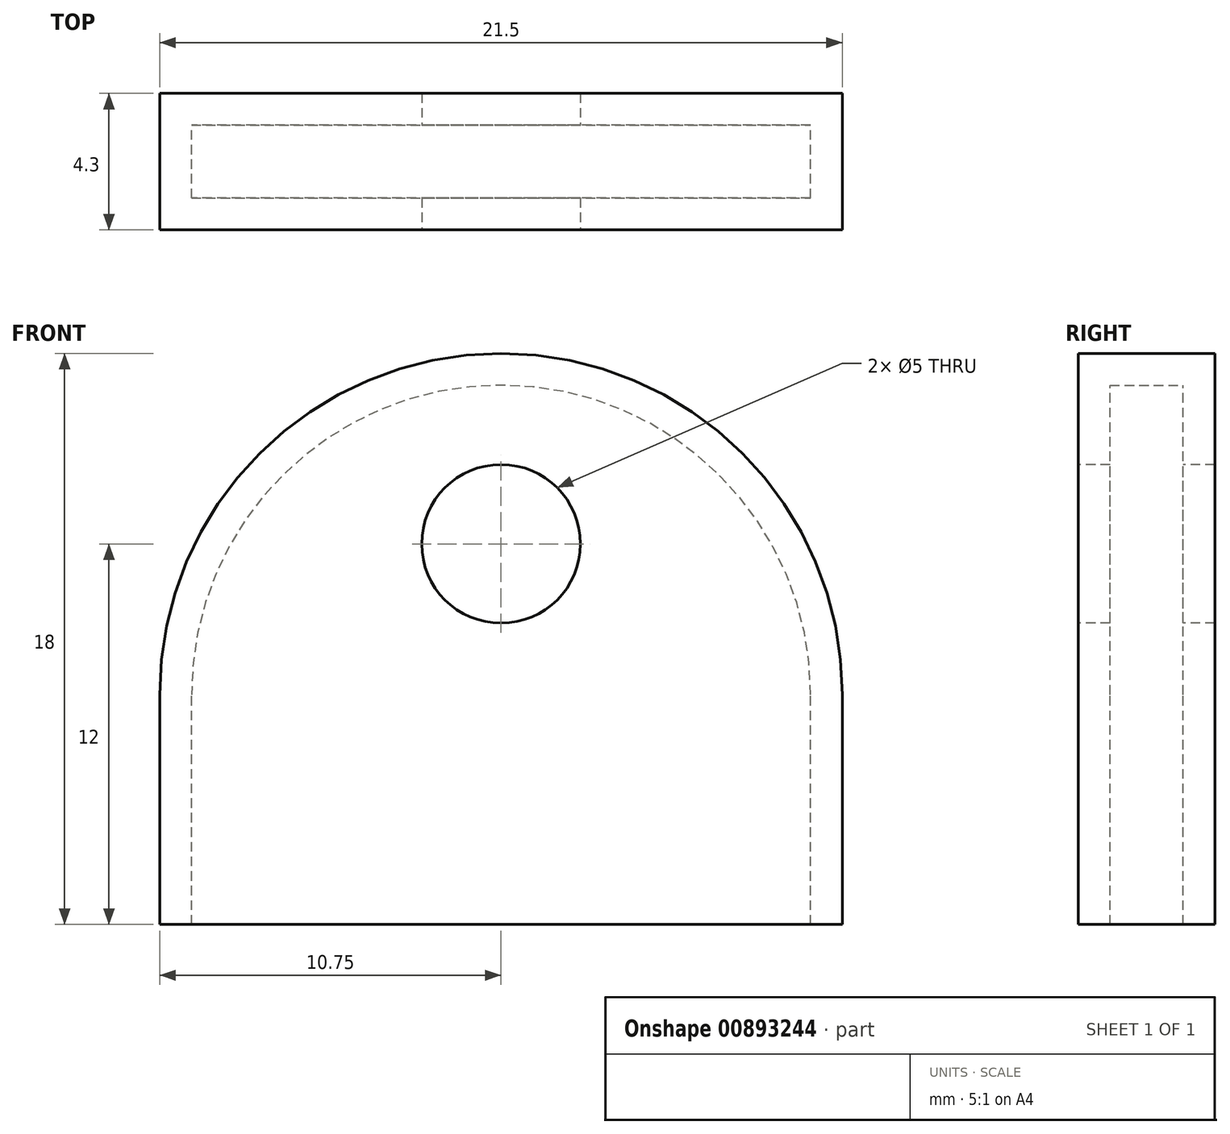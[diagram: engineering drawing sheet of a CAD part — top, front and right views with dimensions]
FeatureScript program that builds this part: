
annotation { "Feature Type Name" : "Feature", "Feature Type Description" : "" }
export const myFeature = defineFeature(function(context is Context, id is Id, definition is map)
    precondition{}
    {
        {
            var Q0;
            Q0=qCreatedBy(makeId("Front.planeOp"),FACE);
            var sketch = newSketch(context, id + "F0", { "sketchPlane" : qUnion([Q0])});
            skLineSegment(sketch, "E0.bottom", {"start": v(0, 0) * mm, "end": v(21.5, 0) * mm});
            skLineSegment(sketch, "E0.top", {"start": v(0, 7.25) * mm, "end": v(21.5, 7.25) * mm});
            skLineSegment(sketch, "E0.left", {"start": v(0, 0) * mm, "end": v(0, 7.25) * mm});
            skLineSegment(sketch, "E0.right", {"start": v(21.5, 0) * mm, "end": v(21.5, 7.25) * mm});
            skArc(sketch, "E1", {"start": v(21.5, 7.25) * mm, "mid": v(10.75, 18) * mm, "end": v(0, 7.25) * mm});
            skSolve(sketch);
        }
        {
            var Q0;
            Q0 = qSketchRegion(id + "F0", true);
            extrude(context, id + "F1", {"entities" : qUnion([Q0]), "depth" : 1 * mm, "offsetDistance" : 25 * mm});
        }
        {
            var Q0;
            Q0=makeQuery(id+"F1.opExtrude","CAP_FACE",FACE,{"disambiguationData":[OSD([sQuery(id+"F0.wireOp",EDGE,"E0.bottom"),sQuery(id+"F0.wireOp",EDGE,"E0.left"),sQuery(id+"F0.wireOp",EDGE,"E0.right"),sQuery(id+"F0.wireOp",EDGE,"E1")])],"isStart":false});
            var sketch = newSketch(context, id + "F2", { "sketchPlane" : qUnion([Q0])});
            skLineSegment(sketch, "E2.0", {"start": v(20.5, 0) * mm, "end": v(20.5, 7.25) * mm});
            skArc(sketch, "E2.1", {"start": v(20.5, 7.25) * mm, "mid": v(10.75, 17) * mm, "end": v(1, 7.25) * mm});
            skLineSegment(sketch, "E2.2", {"start": v(1, 0) * mm, "end": v(1, 7.25) * mm});
            skLineSegment(sketch, "E3", {"start": v(1, 0) * mm, "end": v(0, 0) * mm});
            skLineSegment(sketch, "E4", {"start": v(0, 0) * mm, "end": v(0, 7.25) * mm});
            skLineSegment(sketch, "E5", {"start": v(20.5, 0) * mm, "end": v(21.5, 0) * mm});
            skLineSegment(sketch, "E6", {"start": v(21.5, 0) * mm, "end": v(21.5, 7.25) * mm});
            skArc(sketch, "E7", {"start": v(21.5, 7.25) * mm, "mid": v(10.75, 18) * mm, "end": v(0, 7.25) * mm});
            skSolve(sketch);
        }
        {
            var Q0;
            Q0 = qSketchRegion(id + "F2", true);
            extrude(context, id + "F3", {"entities" : qUnion([Q0]), "operationType" : NewBodyOperationType.ADD, "depth" : 2.3 * mm, "offsetDistance" : 25 * mm});
        }
        {
            var Q0;
            Q0=makeQuery(id+"F3.opExtrude","CAP_FACE",FACE,{"disambiguationData":[OSD([sQuery(id+"F2.wireOp",EDGE,"E2.0"),sQuery(id+"F2.wireOp",EDGE,"E2.1"),sQuery(id+"F2.wireOp",EDGE,"E2.2"),sQuery(id+"F2.wireOp",EDGE,"E3"),sQuery(id+"F2.wireOp",EDGE,"E4"),sQuery(id+"F2.wireOp",EDGE,"E5"),sQuery(id+"F2.wireOp",EDGE,"E6"),sQuery(id+"F2.wireOp",EDGE,"E7")])],"isStart":false});
            var sketch = newSketch(context, id + "F4", { "sketchPlane" : qUnion([Q0])});
            skLineSegment(sketch, "E8", {"start": v(0, 0) * mm, "end": v(21.5, 0) * mm});
            skLineSegment(sketch, "E9", {"start": v(21.5, 0) * mm, "end": v(21.5, 7.25) * mm});
            skLineSegment(sketch, "E10", {"start": v(0, 7.25) * mm, "end": v(0, 0) * mm});
            skArc(sketch, "E11", {"start": v(21.5, 7.25) * mm, "mid": v(10.75, 18) * mm, "end": v(0, 7.25) * mm});
            skSolve(sketch);
        }
        {
            var Q0;
            Q0 = qSketchRegion(id + "F4", true);
            extrude(context, id + "F5", {"entities" : qUnion([Q0]), "operationType" : NewBodyOperationType.ADD, "depth" : 1 * mm, "offsetDistance" : 25 * mm});
        }
        {
            var Q0;
            Q0=makeQuery(id+"F5.opExtrude","CAP_FACE",FACE,{"disambiguationData":[OSD([sQuery(id+"F4.wireOp",EDGE,"E8"),sQuery(id+"F4.wireOp",EDGE,"E9"),sQuery(id+"F4.wireOp",EDGE,"E10"),sQuery(id+"F4.wireOp",EDGE,"E11")])],"isStart":false});
            var sketch = newSketch(context, id + "F6", { "sketchPlane" : qUnion([Q0])});
            skCircle(sketch, "E12", {"center": v(10.75, 12) * mm, "radius": 2.5 * mm});
            skSolve(sketch);
        }
        {
            var Q0;
            Q0 = qSketchRegion(id + "F6", true);
            extrude(context, id + "F7", {"entities" : qUnion([Q0]), "operationType" : NewBodyOperationType.REMOVE, "endBound" : BoundingType.THROUGH_ALL, "oppositeDirection" : true, "depth" : 25 * mm, "offsetDistance" : 25 * mm});
        }
    });
